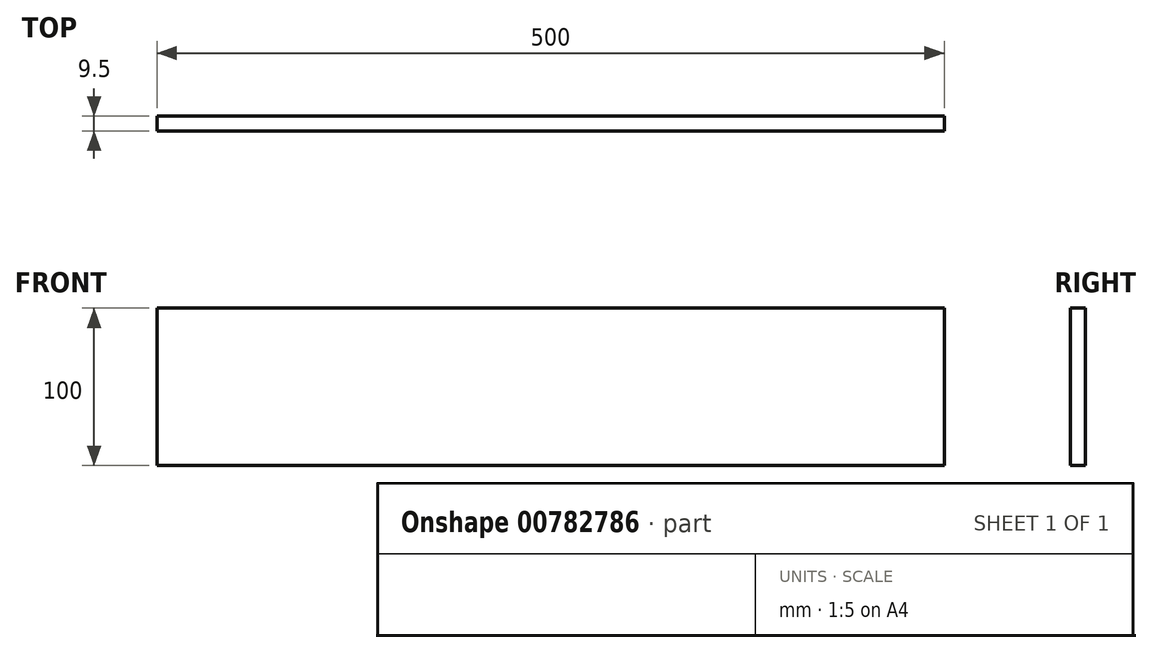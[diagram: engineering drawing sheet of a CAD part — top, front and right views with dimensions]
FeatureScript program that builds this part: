
annotation { "Feature Type Name" : "Feature", "Feature Type Description" : "" }
export const myFeature = defineFeature(function(context is Context, id is Id, definition is map)
    precondition{}
    {
        {
            var Q0;
            Q0=qCreatedBy(makeId("Front.planeOp"),FACE);
            var sketch = newSketch(context, id + "F0", { "sketchPlane" : qUnion([Q0])});
            skLineSegment(sketch, "E0.bottom", {"start": v(-441.27, 80.36) * mm, "end": v(58.73, 80.36) * mm});
            skLineSegment(sketch, "E0.top", {"start": v(-441.27, -19.64) * mm, "end": v(58.73, -19.64) * mm});
            skLineSegment(sketch, "E0.left", {"start": v(-441.27, 80.36) * mm, "end": v(-441.27, -19.64) * mm});
            skLineSegment(sketch, "E0.right", {"start": v(58.73, 80.36) * mm, "end": v(58.73, -19.64) * mm});
            skLineSegment(sketch, "E1.0", {"start": v(-441.27, 65.36) * mm, "end": v(58.73, 65.36) * mm});
            skSolve(sketch);
        }
        {
            var Q0;
            Q0=makeQuery(id+"F0.imprint","IMPRINT",FACE,{"disambiguationData":[TD([[makeQuery(id+"F0.imprint","IMPRINT",EDGE,{"derivedFrom":sQuery(id+"F0.wireOp",EDGE,"E0.bottom")}),-1.0]])]});
            var Q1;
            {var subQ0=sQuery(id+"F0.wireOp",EDGE,"E0.top");Q1=makeQuery(id+"F0.imprint","IMPRINT",FACE,{"disambiguationData":[TD([[makeQuery(id+"F0.imprint","IMPRINT",EDGE,{"derivedFrom":subQ0}),1.0]])]});}
            extrude(context, id + "F1", {"entities" : qUnion([Q0, Q1]), "depth" : 9.5 * mm, "offsetDistance" : 25 * mm});
        }
    });
